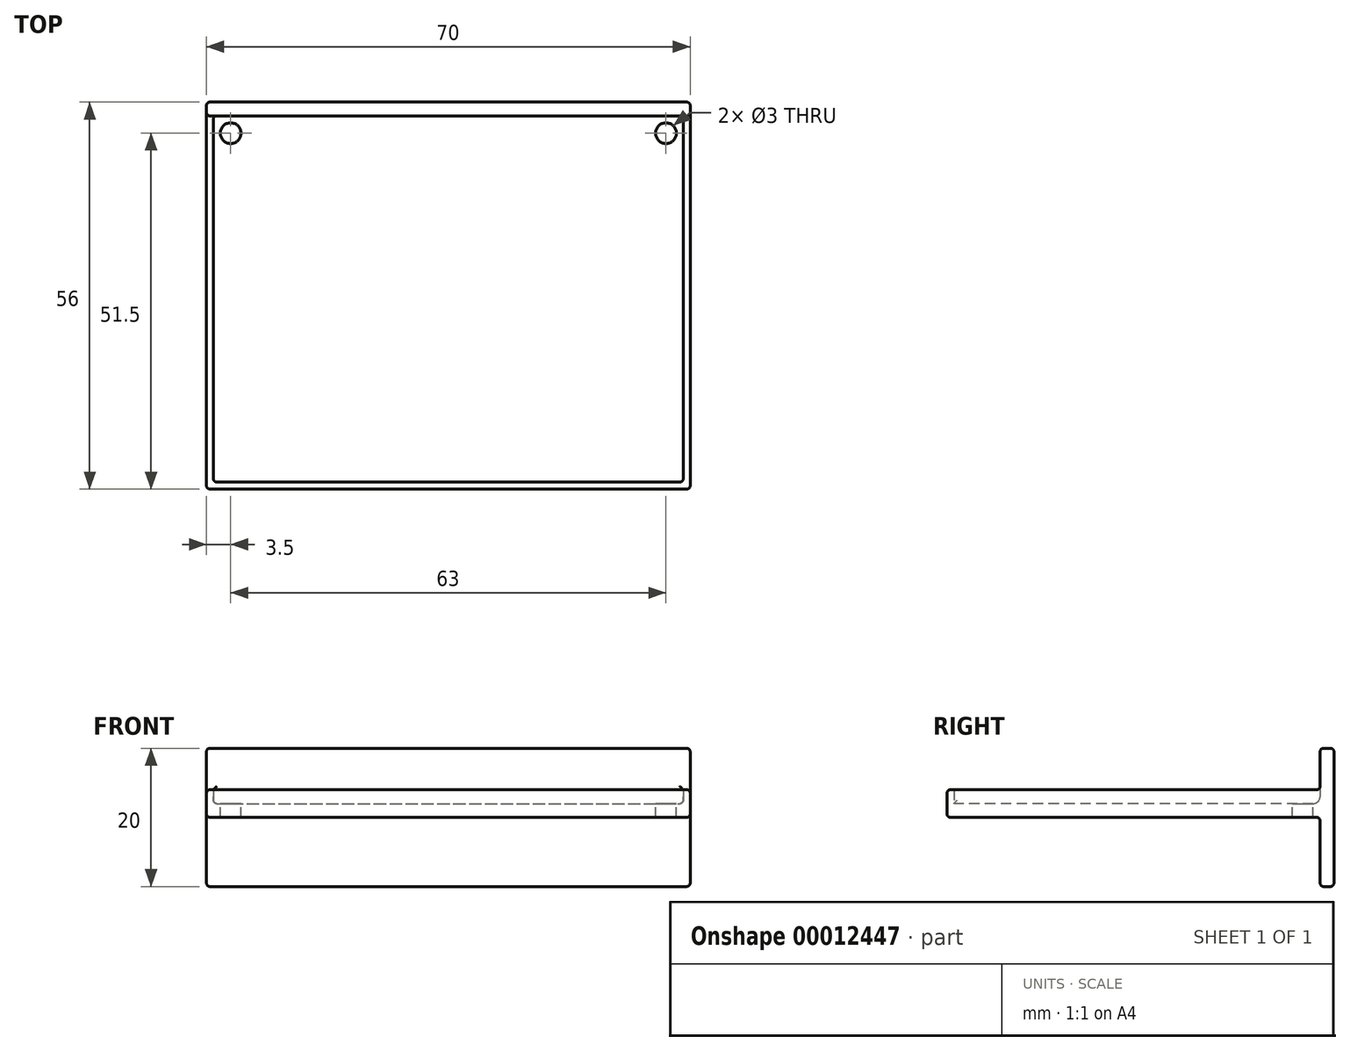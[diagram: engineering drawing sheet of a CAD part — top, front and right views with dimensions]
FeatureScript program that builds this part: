
annotation { "Feature Type Name" : "Feature", "Feature Type Description" : "" }
export const myFeature = defineFeature(function(context is Context, id is Id, definition is map)
    precondition{}
    {
        {
            var Q0;
            Q0=qCreatedBy(makeId("Top.planeOp"),FACE);
            var sketch = newSketch(context, id + "F0", { "sketchPlane" : qUnion([Q0])});
            skLineSegment(sketch, "E0.bottom", {"start": v(0, 0) * mm, "end": v(-70, 0) * mm});
            skLineSegment(sketch, "E0.top", {"start": v(0, -56) * mm, "end": v(-70, -56) * mm});
            skLineSegment(sketch, "E0.left", {"start": v(0, 0) * mm, "end": v(0, -56) * mm});
            skLineSegment(sketch, "E0.right", {"start": v(-70, 0) * mm, "end": v(-70, -56) * mm});
            skSolve(sketch);
        }
        {
            var Q0;
            Q0 = qSketchRegion(id + "F0", true);
            extrude(context, id + "F1", {"entities" : qUnion([Q0]), "depth" : 2 * mm});
        }
        {
            var Q0;
            Q0=makeQuery(id+"F1.opExtrude","CAP_FACE",FACE,{"disambiguationData":[OSD([sQuery(id+"F0.wireOp",EDGE,"E0.bottom"),sQuery(id+"F0.wireOp",EDGE,"E0.top"),sQuery(id+"F0.wireOp",EDGE,"E0.left"),sQuery(id+"F0.wireOp",EDGE,"E0.right")])],"isStart":false});
            var sketch = newSketch(context, id + "F2", { "sketchPlane" : qUnion([Q0])});
            skLineSegment(sketch, "E1.bottom", {"start": v(-70, 0) * mm, "end": v(-69, 0) * mm});
            skLineSegment(sketch, "E1.top", {"start": v(-70, -56) * mm, "end": v(-69, -56) * mm});
            skLineSegment(sketch, "E1.left", {"start": v(-70, 0) * mm, "end": v(-70, -56) * mm});
            skLineSegment(sketch, "E1.right", {"start": v(-69, 0) * mm, "end": v(-69, -56) * mm});
            skLineSegment(sketch, "E2.bottom", {"start": v(-70, -56) * mm, "end": v(0, -56) * mm});
            skLineSegment(sketch, "E2.top", {"start": v(-70, -55) * mm, "end": v(0, -55) * mm});
            skLineSegment(sketch, "E2.left", {"start": v(-70, -56) * mm, "end": v(-70, -55) * mm});
            skLineSegment(sketch, "E2.right", {"start": v(0, -56) * mm, "end": v(0, -55) * mm});
            skLineSegment(sketch, "E3.bottom", {"start": v(0, 0) * mm, "end": v(-1, 0) * mm});
            skLineSegment(sketch, "E3.top", {"start": v(0, -56) * mm, "end": v(-1, -56) * mm});
            skLineSegment(sketch, "E3.left", {"start": v(0, 0) * mm, "end": v(0, -56) * mm});
            skLineSegment(sketch, "E3.right", {"start": v(-1, 0) * mm, "end": v(-1, -56) * mm});
            skLineSegment(sketch, "E4.bottom", {"start": v(-70, 0) * mm, "end": v(0, 0) * mm});
            skLineSegment(sketch, "E4.top", {"start": v(-70, -1) * mm, "end": v(0, -1) * mm});
            skLineSegment(sketch, "E4.left", {"start": v(-70, 0) * mm, "end": v(-70, -1) * mm});
            skLineSegment(sketch, "E4.right", {"start": v(0, 0) * mm, "end": v(0, -1) * mm});
            skSolve(sketch);
        }
        {
            var Q0;
            Q0 = qSketchRegion(id + "F2", true);
            extrude(context, id + "F3", {"entities" : qUnion([Q0]), "operationType" : NewBodyOperationType.ADD, "depth" : 2 * mm});
        }
        {
            var Q0;
            Q0=makeQuery(id+"F1.opExtrude","CAP_FACE",FACE,{"disambiguationData":[OSD([sQuery(id+"F0.wireOp",EDGE,"E0.bottom"),sQuery(id+"F0.wireOp",EDGE,"E0.top"),sQuery(id+"F0.wireOp",EDGE,"E0.left"),sQuery(id+"F0.wireOp",EDGE,"E0.right")])],"isStart":false});
            var sketch = newSketch(context, id + "F4", { "sketchPlane" : qUnion([Q0])});
            skCircle(sketch, "E5", {"center": v(-66.5, -4.5) * mm, "radius": 1.5 * mm});
            skCircle(sketch, "E6", {"center": v(-3.5, -4.5) * mm, "radius": 1.5 * mm});
            skSolve(sketch);
        }
        {
            var Q0;
            Q0 = qSketchRegion(id + "F4", true);
            extrude(context, id + "F5", {"entities" : qUnion([Q0]), "operationType" : NewBodyOperationType.REMOVE, "oppositeDirection" : true, "depth" : 2 * mm});
        }
        {
            var Q0;
            Q0=qCreatedBy(makeId("Front.planeOp"),FACE);
            var sketch = newSketch(context, id + "F6", { "sketchPlane" : qUnion([Q0])});
            skLineSegment(sketch, "E7.bottom", {"start": v(0, 10) * mm, "end": v(-70, 10) * mm});
            skLineSegment(sketch, "E7.top", {"start": v(0, -10) * mm, "end": v(-70, -10) * mm});
            skLineSegment(sketch, "E7.left", {"start": v(0, 10) * mm, "end": v(0, -10) * mm});
            skLineSegment(sketch, "E7.right", {"start": v(-70, 10) * mm, "end": v(-70, -10) * mm});
            skSolve(sketch);
        }
        {
            var Q0;
            Q0 = qSketchRegion(id + "F6", true);
            extrude(context, id + "F7", {"entities" : qUnion([Q0]), "operationType" : NewBodyOperationType.ADD, "depth" : 2 * mm});
        }
        {
            var Q0;
            Q0=makeQuery(id+"F3.opExtrude","CAP_EDGE",EDGE,{"disambiguationData":[OSD([sQuery(id+"F2.wireOp",EDGE,"E4.top")])],"isStart":true});
            var Q1;
            Q1=makeQuery(id+"F3.opExtrude","CAP_EDGE",EDGE,{"disambiguationData":[OSD([sQuery(id+"F2.wireOp",EDGE,"E1.right")])],"isStart":true});
            var Q2;
            Q2=makeQuery(id+"F3.opExtrude","CAP_EDGE",EDGE,{"disambiguationData":[OSD([sQuery(id+"F2.wireOp",EDGE,"E3.right")])],"isStart":true});
            var Q3;
            Q3=makeQuery(id+"F3.opExtrude","CAP_EDGE",EDGE,{"disambiguationData":[OSD([sQuery(id+"F2.wireOp",EDGE,"E2.top")])],"isStart":true});
            var Q4;
            Q4=makeQuery(id+"F7.boolean.opBoolean","INTERSECT",EDGE,{"derivedFrom":[makeQuery(id+"F1.opExtrude","CAP_FACE",FACE,{"disambiguationData":[OSD([sQuery(id+"F0.wireOp",EDGE,"E0.bottom"),sQuery(id+"F0.wireOp",EDGE,"E0.top"),sQuery(id+"F0.wireOp",EDGE,"E0.left"),sQuery(id+"F0.wireOp",EDGE,"E0.right")])],"isStart":false}),makeQuery(id+"F7.opExtrude","CAP_FACE",FACE,{"disambiguationData":[OSD([sQuery(id+"F6.wireOp",EDGE,"E7.bottom"),sQuery(id+"F6.wireOp",EDGE,"E7.top"),sQuery(id+"F6.wireOp",EDGE,"E7.left"),sQuery(id+"F6.wireOp",EDGE,"E7.right")])],"isStart":false})]});
            fillet(context, id + "F8", {"entities" : qUnion([Q0, Q1, Q2, Q3, Q4]), "radius" : 1 * mm, "tangentPropagation" : true, "allowEdgeOverflow" : false});
        }
        {
            var Q0;
            Q0=makeQuery(id+"F3.opExtrude","CAP_EDGE",EDGE,{"disambiguationData":[OSD([sQuery(id+"F2.wireOp",EDGE,"E4.bottom")])],"isStart":false});
            var Q1;
            {var subQ0=sQuery(id+"F2.wireOp",EDGE,"E4.top");Q1=makeQuery(id+"F8.opFillet","BLEND_EDGE",EDGE,{"blendedFrom":[makeQuery(id+"F3.opExtrude","CAP_EDGE",EDGE,{"disambiguationData":[OSD([subQ0])],"isStart":true}),makeQuery(id+"F3.opExtrude","CAP_FACE",FACE,{"disambiguationData":[OSD([sQuery(id+"F2.wireOp",EDGE,"E1.left"),sQuery(id+"F2.wireOp",EDGE,"E1.right"),sQuery(id+"F2.wireOp",EDGE,"E2.bottom"),sQuery(id+"F2.wireOp",EDGE,"E2.top"),sQuery(id+"F2.wireOp",EDGE,"E2.left"),sQuery(id+"F2.wireOp",EDGE,"E3.top"),sQuery(id+"F2.wireOp",EDGE,"E3.left"),sQuery(id+"F2.wireOp",EDGE,"E3.right"),sQuery(id+"F2.wireOp",EDGE,"E4.bottom"),subQ0,sQuery(id+"F2.wireOp",EDGE,"E4.left"),sQuery(id+"F2.wireOp",EDGE,"E4.right")])],"isStart":false})],"blendedInto":[makeQuery(id+"F3.opExtrude","CAP_FACE",FACE,{"disambiguationData":[OSD([sQuery(id+"F2.wireOp",EDGE,"E1.left"),sQuery(id+"F2.wireOp",EDGE,"E1.right"),sQuery(id+"F2.wireOp",EDGE,"E2.bottom"),sQuery(id+"F2.wireOp",EDGE,"E2.top"),sQuery(id+"F2.wireOp",EDGE,"E2.left"),sQuery(id+"F2.wireOp",EDGE,"E3.top"),sQuery(id+"F2.wireOp",EDGE,"E3.left"),sQuery(id+"F2.wireOp",EDGE,"E3.right"),sQuery(id+"F2.wireOp",EDGE,"E4.bottom"),subQ0,sQuery(id+"F2.wireOp",EDGE,"E4.left"),sQuery(id+"F2.wireOp",EDGE,"E4.right")])],"isStart":false})]});}
            var Q2;
            Q2=makeQuery(id+"F3.opExtrude","CAP_EDGE",EDGE,{"disambiguationData":[OSD([sQuery(id+"F2.wireOp",EDGE,"E1.left"),sQuery(id+"F2.wireOp",EDGE,"E2.left"),sQuery(id+"F2.wireOp",EDGE,"E4.left")])],"isStart":false});
            var Q3;
            {var subQ0=sQuery(id+"F2.wireOp",EDGE,"E1.right");Q3=makeQuery(id+"F8.opFillet","BLEND_EDGE",EDGE,{"blendedFrom":[makeQuery(id+"F3.opExtrude","CAP_EDGE",EDGE,{"disambiguationData":[OSD([subQ0])],"isStart":true}),makeQuery(id+"F3.opExtrude","CAP_FACE",FACE,{"disambiguationData":[OSD([sQuery(id+"F2.wireOp",EDGE,"E1.left"),subQ0,sQuery(id+"F2.wireOp",EDGE,"E2.bottom"),sQuery(id+"F2.wireOp",EDGE,"E2.top"),sQuery(id+"F2.wireOp",EDGE,"E2.left"),sQuery(id+"F2.wireOp",EDGE,"E3.top"),sQuery(id+"F2.wireOp",EDGE,"E3.left"),sQuery(id+"F2.wireOp",EDGE,"E3.right"),sQuery(id+"F2.wireOp",EDGE,"E4.bottom"),sQuery(id+"F2.wireOp",EDGE,"E4.top"),sQuery(id+"F2.wireOp",EDGE,"E4.left"),sQuery(id+"F2.wireOp",EDGE,"E4.right")])],"isStart":false})],"blendedInto":[makeQuery(id+"F3.opExtrude","CAP_FACE",FACE,{"disambiguationData":[OSD([sQuery(id+"F2.wireOp",EDGE,"E1.left"),subQ0,sQuery(id+"F2.wireOp",EDGE,"E2.bottom"),sQuery(id+"F2.wireOp",EDGE,"E2.top"),sQuery(id+"F2.wireOp",EDGE,"E2.left"),sQuery(id+"F2.wireOp",EDGE,"E3.top"),sQuery(id+"F2.wireOp",EDGE,"E3.left"),sQuery(id+"F2.wireOp",EDGE,"E3.right"),sQuery(id+"F2.wireOp",EDGE,"E4.bottom"),sQuery(id+"F2.wireOp",EDGE,"E4.top"),sQuery(id+"F2.wireOp",EDGE,"E4.left"),sQuery(id+"F2.wireOp",EDGE,"E4.right")])],"isStart":false})]});}
            var Q4;
            {var subQ0=sQuery(id+"F2.wireOp",EDGE,"E3.right");Q4=makeQuery(id+"F8.opFillet","BLEND_EDGE",EDGE,{"blendedFrom":[makeQuery(id+"F3.opExtrude","CAP_EDGE",EDGE,{"disambiguationData":[OSD([subQ0])],"isStart":true}),makeQuery(id+"F3.opExtrude","CAP_FACE",FACE,{"disambiguationData":[OSD([sQuery(id+"F2.wireOp",EDGE,"E1.left"),sQuery(id+"F2.wireOp",EDGE,"E1.right"),sQuery(id+"F2.wireOp",EDGE,"E2.bottom"),sQuery(id+"F2.wireOp",EDGE,"E2.top"),sQuery(id+"F2.wireOp",EDGE,"E2.left"),sQuery(id+"F2.wireOp",EDGE,"E3.top"),sQuery(id+"F2.wireOp",EDGE,"E3.left"),subQ0,sQuery(id+"F2.wireOp",EDGE,"E4.bottom"),sQuery(id+"F2.wireOp",EDGE,"E4.top"),sQuery(id+"F2.wireOp",EDGE,"E4.left"),sQuery(id+"F2.wireOp",EDGE,"E4.right")])],"isStart":false})],"blendedInto":[makeQuery(id+"F3.opExtrude","CAP_FACE",FACE,{"disambiguationData":[OSD([sQuery(id+"F2.wireOp",EDGE,"E1.left"),sQuery(id+"F2.wireOp",EDGE,"E1.right"),sQuery(id+"F2.wireOp",EDGE,"E2.bottom"),sQuery(id+"F2.wireOp",EDGE,"E2.top"),sQuery(id+"F2.wireOp",EDGE,"E2.left"),sQuery(id+"F2.wireOp",EDGE,"E3.top"),sQuery(id+"F2.wireOp",EDGE,"E3.left"),subQ0,sQuery(id+"F2.wireOp",EDGE,"E4.bottom"),sQuery(id+"F2.wireOp",EDGE,"E4.top"),sQuery(id+"F2.wireOp",EDGE,"E4.left"),sQuery(id+"F2.wireOp",EDGE,"E4.right")])],"isStart":false})]});}
            var Q5;
            Q5=makeQuery(id+"F3.opExtrude","CAP_EDGE",EDGE,{"disambiguationData":[OSD([sQuery(id+"F2.wireOp",EDGE,"E3.left"),sQuery(id+"F2.wireOp",EDGE,"E4.right")])],"isStart":false});
            var Q6;
            {var subQ0=sQuery(id+"F2.wireOp",EDGE,"E2.top");Q6=makeQuery(id+"F8.opFillet","BLEND_EDGE",EDGE,{"blendedFrom":[makeQuery(id+"F3.opExtrude","CAP_EDGE",EDGE,{"disambiguationData":[OSD([subQ0])],"isStart":true}),makeQuery(id+"F3.opExtrude","CAP_FACE",FACE,{"disambiguationData":[OSD([sQuery(id+"F2.wireOp",EDGE,"E1.left"),sQuery(id+"F2.wireOp",EDGE,"E1.right"),sQuery(id+"F2.wireOp",EDGE,"E2.bottom"),subQ0,sQuery(id+"F2.wireOp",EDGE,"E2.left"),sQuery(id+"F2.wireOp",EDGE,"E3.top"),sQuery(id+"F2.wireOp",EDGE,"E3.left"),sQuery(id+"F2.wireOp",EDGE,"E3.right"),sQuery(id+"F2.wireOp",EDGE,"E4.bottom"),sQuery(id+"F2.wireOp",EDGE,"E4.top"),sQuery(id+"F2.wireOp",EDGE,"E4.left"),sQuery(id+"F2.wireOp",EDGE,"E4.right")])],"isStart":false})],"blendedInto":[makeQuery(id+"F3.opExtrude","CAP_FACE",FACE,{"disambiguationData":[OSD([sQuery(id+"F2.wireOp",EDGE,"E1.left"),sQuery(id+"F2.wireOp",EDGE,"E1.right"),sQuery(id+"F2.wireOp",EDGE,"E2.bottom"),subQ0,sQuery(id+"F2.wireOp",EDGE,"E2.left"),sQuery(id+"F2.wireOp",EDGE,"E3.top"),sQuery(id+"F2.wireOp",EDGE,"E3.left"),sQuery(id+"F2.wireOp",EDGE,"E3.right"),sQuery(id+"F2.wireOp",EDGE,"E4.bottom"),sQuery(id+"F2.wireOp",EDGE,"E4.top"),sQuery(id+"F2.wireOp",EDGE,"E4.left"),sQuery(id+"F2.wireOp",EDGE,"E4.right")])],"isStart":false})]});}
            var Q7;
            Q7=makeQuery(id+"F3.opExtrude","CAP_EDGE",EDGE,{"disambiguationData":[OSD([sQuery(id+"F2.wireOp",EDGE,"E2.bottom"),sQuery(id+"F2.wireOp",EDGE,"E3.top")])],"isStart":false});
            var Q8;
            Q8=makeQuery(id+"F3.boolean.opBoolean","MERGE",EDGE,{"derivedFrom":[makeQuery(id+"F1.opExtrude","SWEPT_EDGE",EDGE,{"disambiguationData":[OSD([sQuery(id+"F0.wireOp",EDGE,"E0.bottom"),sQuery(id+"F0.wireOp",EDGE,"E0.right")])]}),makeQuery(id+"F3.opExtrude","SWEPT_EDGE",EDGE,{"disambiguationData":[OSD([sQuery(id+"F2.wireOp",EDGE,"E4.bottom"),sQuery(id+"F2.wireOp",EDGE,"E4.left")])]})]});
            var Q9;
            Q9=makeQuery(id+"F3.boolean.opBoolean","MERGE",EDGE,{"derivedFrom":[makeQuery(id+"F1.opExtrude","SWEPT_EDGE",EDGE,{"disambiguationData":[OSD([sQuery(id+"F0.wireOp",EDGE,"E0.top"),sQuery(id+"F0.wireOp",EDGE,"E0.right")])]}),makeQuery(id+"F3.opExtrude","SWEPT_EDGE",EDGE,{"disambiguationData":[OSD([sQuery(id+"F2.wireOp",EDGE,"E2.bottom"),sQuery(id+"F2.wireOp",EDGE,"E2.left")])]})]});
            var Q10;
            Q10=makeQuery(id+"F3.boolean.opBoolean","MERGE",EDGE,{"derivedFrom":[makeQuery(id+"F1.opExtrude","SWEPT_EDGE",EDGE,{"disambiguationData":[OSD([sQuery(id+"F0.wireOp",EDGE,"E0.bottom"),sQuery(id+"F0.wireOp",EDGE,"E0.left")])]}),makeQuery(id+"F3.opExtrude","SWEPT_EDGE",EDGE,{"disambiguationData":[OSD([sQuery(id+"F2.wireOp",EDGE,"E4.bottom"),sQuery(id+"F2.wireOp",EDGE,"E4.right")])]})]});
            var Q11;
            Q11=makeQuery(id+"F3.boolean.opBoolean","MERGE",EDGE,{"derivedFrom":[makeQuery(id+"F1.opExtrude","SWEPT_EDGE",EDGE,{"disambiguationData":[OSD([sQuery(id+"F0.wireOp",EDGE,"E0.top"),sQuery(id+"F0.wireOp",EDGE,"E0.left")])]}),makeQuery(id+"F3.opExtrude","SWEPT_EDGE",EDGE,{"disambiguationData":[OSD([sQuery(id+"F2.wireOp",EDGE,"E3.top"),sQuery(id+"F2.wireOp",EDGE,"E3.left")])]})]});
            var Q12;
            Q12=makeQuery(id+"F5.boolean.opBoolean","COPY",EDGE,{"derivedFrom":makeQuery(id+"F5.opExtrude","CAP_EDGE",EDGE,{"disambiguationData":[OSD([sQuery(id+"F4.wireOp",EDGE,"E5")])],"isStart":true})});
            var Q13;
            Q13=makeQuery(id+"F5.boolean.opBoolean","COPY",EDGE,{"derivedFrom":makeQuery(id+"F5.opExtrude","CAP_EDGE",EDGE,{"disambiguationData":[OSD([sQuery(id+"F4.wireOp",EDGE,"E6")])],"isStart":true})});
            var Q14;
            Q14=makeQuery(id+"F5.boolean.opBoolean","COPY",EDGE,{"derivedFrom":makeQuery(id+"F5.opExtrude","CAP_EDGE",EDGE,{"disambiguationData":[OSD([sQuery(id+"F4.wireOp",EDGE,"E5")])],"isStart":false})});
            var Q15;
            Q15=makeQuery(id+"F5.boolean.opBoolean","COPY",EDGE,{"derivedFrom":makeQuery(id+"F5.opExtrude","CAP_EDGE",EDGE,{"disambiguationData":[OSD([sQuery(id+"F4.wireOp",EDGE,"E6")])],"isStart":false})});
            var Q16;
            Q16=makeQuery(id+"F1.opExtrude","CAP_EDGE",EDGE,{"disambiguationData":[OSD([sQuery(id+"F0.wireOp",EDGE,"E0.top")])],"isStart":true});
            var Q17;
            Q17=makeQuery(id+"F1.opExtrude","CAP_EDGE",EDGE,{"disambiguationData":[OSD([sQuery(id+"F0.wireOp",EDGE,"E0.left")])],"isStart":true});
            var Q18;
            Q18=makeQuery(id+"F1.opExtrude","CAP_EDGE",EDGE,{"disambiguationData":[OSD([sQuery(id+"F0.wireOp",EDGE,"E0.bottom")])],"isStart":true});
            var Q19;
            Q19=makeQuery(id+"F1.opExtrude","CAP_EDGE",EDGE,{"disambiguationData":[OSD([sQuery(id+"F0.wireOp",EDGE,"E0.right")])],"isStart":true});
            var Q20;
            Q20=makeQuery(id+"F8.opFillet","BLEND_EDGE",EDGE,{"blendedFrom":[makeQuery(id+"F3.opExtrude","CAP_EDGE",EDGE,{"disambiguationData":[OSD([sQuery(id+"F2.wireOp",EDGE,"E3.right")])],"isStart":true}),makeQuery(id+"F7.boolean.opBoolean","INTERSECT",EDGE,{"derivedFrom":[makeQuery(id+"F1.opExtrude","CAP_FACE",FACE,{"disambiguationData":[OSD([sQuery(id+"F0.wireOp",EDGE,"E0.bottom"),sQuery(id+"F0.wireOp",EDGE,"E0.top"),sQuery(id+"F0.wireOp",EDGE,"E0.left"),sQuery(id+"F0.wireOp",EDGE,"E0.right")])],"isStart":false}),makeQuery(id+"F7.opExtrude","CAP_FACE",FACE,{"disambiguationData":[OSD([sQuery(id+"F6.wireOp",EDGE,"E7.bottom"),sQuery(id+"F6.wireOp",EDGE,"E7.top"),sQuery(id+"F6.wireOp",EDGE,"E7.left"),sQuery(id+"F6.wireOp",EDGE,"E7.right")])],"isStart":false})]})],"blendedInto":[]});
            var Q21;
            Q21=makeQuery(id+"F7.boolean.opBoolean","INTERSECT",EDGE,{"derivedFrom":[makeQuery(id+"F3.opExtrude","SWEPT_FACE",FACE,{"disambiguationData":[OSD([sQuery(id+"F2.wireOp",EDGE,"E3.right")])]}),makeQuery(id+"F7.opExtrude","CAP_FACE",FACE,{"disambiguationData":[OSD([sQuery(id+"F6.wireOp",EDGE,"E7.bottom"),sQuery(id+"F6.wireOp",EDGE,"E7.top"),sQuery(id+"F6.wireOp",EDGE,"E7.left"),sQuery(id+"F6.wireOp",EDGE,"E7.right")])],"isStart":false})]});
            var Q22;
            Q22=makeQuery(id+"F7.boolean.opBoolean","INTERSECT",EDGE,{"disambiguationData":[OD(1.0)],"derivedFrom":[makeQuery(id+"F3.opExtrude","CAP_FACE",FACE,{"disambiguationData":[OSD([sQuery(id+"F2.wireOp",EDGE,"E1.left"),sQuery(id+"F2.wireOp",EDGE,"E1.right"),sQuery(id+"F2.wireOp",EDGE,"E2.bottom"),sQuery(id+"F2.wireOp",EDGE,"E2.top"),sQuery(id+"F2.wireOp",EDGE,"E2.left"),sQuery(id+"F2.wireOp",EDGE,"E3.top"),sQuery(id+"F2.wireOp",EDGE,"E3.left"),sQuery(id+"F2.wireOp",EDGE,"E3.right"),sQuery(id+"F2.wireOp",EDGE,"E4.bottom"),sQuery(id+"F2.wireOp",EDGE,"E4.top"),sQuery(id+"F2.wireOp",EDGE,"E4.left"),sQuery(id+"F2.wireOp",EDGE,"E4.right")])],"isStart":false}),makeQuery(id+"F7.opExtrude","CAP_FACE",FACE,{"disambiguationData":[OSD([sQuery(id+"F6.wireOp",EDGE,"E7.bottom"),sQuery(id+"F6.wireOp",EDGE,"E7.top"),sQuery(id+"F6.wireOp",EDGE,"E7.left"),sQuery(id+"F6.wireOp",EDGE,"E7.right")])],"isStart":false})]});
            var Q23;
            Q23=makeQuery(id+"F7.opExtrude","CAP_EDGE",EDGE,{"disambiguationData":[OSD([sQuery(id+"F6.wireOp",EDGE,"E7.bottom")])],"isStart":true});
            var Q24;
            Q24=makeQuery(id+"F7.opExtrude","SWEPT_EDGE",EDGE,{"disambiguationData":[OSD([sQuery(id+"F6.wireOp",EDGE,"E7.bottom"),sQuery(id+"F6.wireOp",EDGE,"E7.left")])]});
            var Q25;
            Q25=makeQuery(id+"F7.opExtrude","CAP_EDGE",EDGE,{"disambiguationData":[OSD([sQuery(id+"F6.wireOp",EDGE,"E7.bottom")])],"isStart":false});
            var Q26;
            {var subQ0=sQuery(id+"F6.wireOp",EDGE,"E7.bottom");var subQ3=sQuery(id+"F6.wireOp",EDGE,"E7.left");Q26=makeQuery(id+"F7.boolean.opBoolean","SPLIT",EDGE,{"disambiguationData":[TD([makeQuery(id+"F7.opExtrude","SWEPT_FACE",FACE,{"disambiguationData":[OSD([subQ0])]})])],"derivedFrom":makeQuery(id+"F7.opExtrude","CAP_EDGE",EDGE,{"disambiguationData":[OSD([subQ3])],"isStart":false})});}
            var Q27;
            Q27=makeQuery(id+"F8.opFillet","BLEND_EDGE",EDGE,{"blendedFrom":[makeQuery(id+"F3.opExtrude","CAP_EDGE",EDGE,{"disambiguationData":[OSD([sQuery(id+"F2.wireOp",EDGE,"E2.top")])],"isStart":true}),makeQuery(id+"F3.opExtrude","CAP_EDGE",EDGE,{"disambiguationData":[OSD([sQuery(id+"F2.wireOp",EDGE,"E1.right")])],"isStart":true})],"blendedInto":[]});
            var Q28;
            Q28=makeQuery(id+"F3.opExtrude","SWEPT_EDGE",EDGE,{"disambiguationData":[OSD([sQuery(id+"F2.wireOp",EDGE,"E1.right"),sQuery(id+"F2.wireOp",EDGE,"E2.top")])]});
            var Q29;
            Q29=makeQuery(id+"F8.opFillet","BLEND_EDGE",EDGE,{"blendedFrom":[makeQuery(id+"F3.opExtrude","CAP_EDGE",EDGE,{"disambiguationData":[OSD([sQuery(id+"F2.wireOp",EDGE,"E1.right")])],"isStart":true}),makeQuery(id+"F7.boolean.opBoolean","INTERSECT",EDGE,{"derivedFrom":[makeQuery(id+"F1.opExtrude","CAP_FACE",FACE,{"disambiguationData":[OSD([sQuery(id+"F0.wireOp",EDGE,"E0.bottom"),sQuery(id+"F0.wireOp",EDGE,"E0.top"),sQuery(id+"F0.wireOp",EDGE,"E0.left"),sQuery(id+"F0.wireOp",EDGE,"E0.right")])],"isStart":false}),makeQuery(id+"F7.opExtrude","CAP_FACE",FACE,{"disambiguationData":[OSD([sQuery(id+"F6.wireOp",EDGE,"E7.bottom"),sQuery(id+"F6.wireOp",EDGE,"E7.top"),sQuery(id+"F6.wireOp",EDGE,"E7.left"),sQuery(id+"F6.wireOp",EDGE,"E7.right")])],"isStart":false})]})],"blendedInto":[]});
            var Q30;
            Q30=makeQuery(id+"F7.boolean.opBoolean","INTERSECT",EDGE,{"derivedFrom":[makeQuery(id+"F3.opExtrude","SWEPT_FACE",FACE,{"disambiguationData":[OSD([sQuery(id+"F2.wireOp",EDGE,"E1.right")])]}),makeQuery(id+"F7.opExtrude","CAP_FACE",FACE,{"disambiguationData":[OSD([sQuery(id+"F6.wireOp",EDGE,"E7.bottom"),sQuery(id+"F6.wireOp",EDGE,"E7.top"),sQuery(id+"F6.wireOp",EDGE,"E7.left"),sQuery(id+"F6.wireOp",EDGE,"E7.right")])],"isStart":false})]});
            var Q31;
            Q31=makeQuery(id+"F7.boolean.opBoolean","INTERSECT",EDGE,{"disambiguationData":[OD(0.0)],"derivedFrom":[makeQuery(id+"F3.opExtrude","CAP_FACE",FACE,{"disambiguationData":[OSD([sQuery(id+"F2.wireOp",EDGE,"E1.left"),sQuery(id+"F2.wireOp",EDGE,"E1.right"),sQuery(id+"F2.wireOp",EDGE,"E2.bottom"),sQuery(id+"F2.wireOp",EDGE,"E2.top"),sQuery(id+"F2.wireOp",EDGE,"E2.left"),sQuery(id+"F2.wireOp",EDGE,"E3.top"),sQuery(id+"F2.wireOp",EDGE,"E3.left"),sQuery(id+"F2.wireOp",EDGE,"E3.right"),sQuery(id+"F2.wireOp",EDGE,"E4.bottom"),sQuery(id+"F2.wireOp",EDGE,"E4.top"),sQuery(id+"F2.wireOp",EDGE,"E4.left"),sQuery(id+"F2.wireOp",EDGE,"E4.right")])],"isStart":false}),makeQuery(id+"F7.opExtrude","CAP_FACE",FACE,{"disambiguationData":[OSD([sQuery(id+"F6.wireOp",EDGE,"E7.bottom"),sQuery(id+"F6.wireOp",EDGE,"E7.top"),sQuery(id+"F6.wireOp",EDGE,"E7.left"),sQuery(id+"F6.wireOp",EDGE,"E7.right")])],"isStart":false})]});
            var Q32;
            {var subQ0=sQuery(id+"F6.wireOp",EDGE,"E7.bottom");var subQ4=sQuery(id+"F6.wireOp",EDGE,"E7.right");Q32=makeQuery(id+"F7.boolean.opBoolean","SPLIT",EDGE,{"disambiguationData":[TD([makeQuery(id+"F7.opExtrude","SWEPT_FACE",FACE,{"disambiguationData":[OSD([subQ0])]})])],"derivedFrom":makeQuery(id+"F7.opExtrude","CAP_EDGE",EDGE,{"disambiguationData":[OSD([subQ4])],"isStart":false})});}
            var Q33;
            Q33=makeQuery(id+"F7.opExtrude","SWEPT_EDGE",EDGE,{"disambiguationData":[OSD([sQuery(id+"F6.wireOp",EDGE,"E7.bottom"),sQuery(id+"F6.wireOp",EDGE,"E7.right")])]});
            var Q34;
            Q34=makeQuery(id+"F8.opFillet","BLEND_EDGE",EDGE,{"blendedFrom":[makeQuery(id+"F3.opExtrude","CAP_EDGE",EDGE,{"disambiguationData":[OSD([sQuery(id+"F2.wireOp",EDGE,"E2.top")])],"isStart":true}),makeQuery(id+"F3.opExtrude","CAP_EDGE",EDGE,{"disambiguationData":[OSD([sQuery(id+"F2.wireOp",EDGE,"E3.right")])],"isStart":true})],"blendedInto":[]});
            var Q35;
            Q35=makeQuery(id+"F3.opExtrude","SWEPT_EDGE",EDGE,{"disambiguationData":[OSD([sQuery(id+"F2.wireOp",EDGE,"E2.top"),sQuery(id+"F2.wireOp",EDGE,"E3.right")])]});
            var Q36;
            {var subQ0=sQuery(id+"F6.wireOp",EDGE,"E7.right");var subQ1=sQuery(id+"F6.wireOp",EDGE,"E7.top");Q36=makeQuery(id+"F7.boolean.opBoolean","SPLIT",EDGE,{"disambiguationData":[TD([makeQuery(id+"F7.opExtrude","SWEPT_FACE",FACE,{"disambiguationData":[OSD([subQ1])]})])],"derivedFrom":makeQuery(id+"F7.opExtrude","CAP_EDGE",EDGE,{"disambiguationData":[OSD([subQ0])],"isStart":false})});}
            var Q37;
            Q37=makeQuery(id+"F7.opExtrude","SWEPT_EDGE",EDGE,{"disambiguationData":[OSD([sQuery(id+"F6.wireOp",EDGE,"E7.top"),sQuery(id+"F6.wireOp",EDGE,"E7.right")])]});
            var Q38;
            Q38=makeQuery(id+"F7.opExtrude","CAP_EDGE",EDGE,{"disambiguationData":[OSD([sQuery(id+"F6.wireOp",EDGE,"E7.top")])],"isStart":false});
            var Q39;
            Q39=makeQuery(id+"F7.opExtrude","CAP_EDGE",EDGE,{"disambiguationData":[OSD([sQuery(id+"F6.wireOp",EDGE,"E7.top")])],"isStart":true});
            var Q40;
            {var subQ0=sQuery(id+"F6.wireOp",EDGE,"E7.left");var subQ1=sQuery(id+"F6.wireOp",EDGE,"E7.top");Q40=makeQuery(id+"F7.boolean.opBoolean","SPLIT",EDGE,{"disambiguationData":[TD([makeQuery(id+"F7.opExtrude","SWEPT_FACE",FACE,{"disambiguationData":[OSD([subQ1])]})])],"derivedFrom":makeQuery(id+"F7.opExtrude","CAP_EDGE",EDGE,{"disambiguationData":[OSD([subQ0])],"isStart":false})});}
            var Q41;
            Q41=makeQuery(id+"F7.opExtrude","SWEPT_EDGE",EDGE,{"disambiguationData":[OSD([sQuery(id+"F6.wireOp",EDGE,"E7.top"),sQuery(id+"F6.wireOp",EDGE,"E7.left")])]});
            var Q42;
            Q42=makeQuery(id+"F7.boolean.opBoolean","INTERSECT",EDGE,{"derivedFrom":[makeQuery(id+"F1.opExtrude","CAP_FACE",FACE,{"disambiguationData":[OSD([sQuery(id+"F0.wireOp",EDGE,"E0.bottom"),sQuery(id+"F0.wireOp",EDGE,"E0.top"),sQuery(id+"F0.wireOp",EDGE,"E0.left"),sQuery(id+"F0.wireOp",EDGE,"E0.right")])],"isStart":true}),makeQuery(id+"F7.opExtrude","CAP_FACE",FACE,{"disambiguationData":[OSD([sQuery(id+"F6.wireOp",EDGE,"E7.bottom"),sQuery(id+"F6.wireOp",EDGE,"E7.top"),sQuery(id+"F6.wireOp",EDGE,"E7.left"),sQuery(id+"F6.wireOp",EDGE,"E7.right")])],"isStart":false})]});
            fillet(context, id + "F9", {"entities" : qUnion([Q0, Q1, Q2, Q3, Q4, Q5, Q6, Q7, Q8, Q9, Q10, Q11, Q12, Q13, Q14, Q15, Q16, Q17, Q18, Q19, Q20, Q21, Q22, Q23, Q24, Q25, Q26, Q27, Q28, Q29, Q30, Q31, Q32, Q33, Q34, Q35, Q36, Q37, Q38, Q39, Q40, Q41, Q42]), "radius" : 0.5 * mm, "tangentPropagation" : true, "allowEdgeOverflow" : false});
        }
    });
